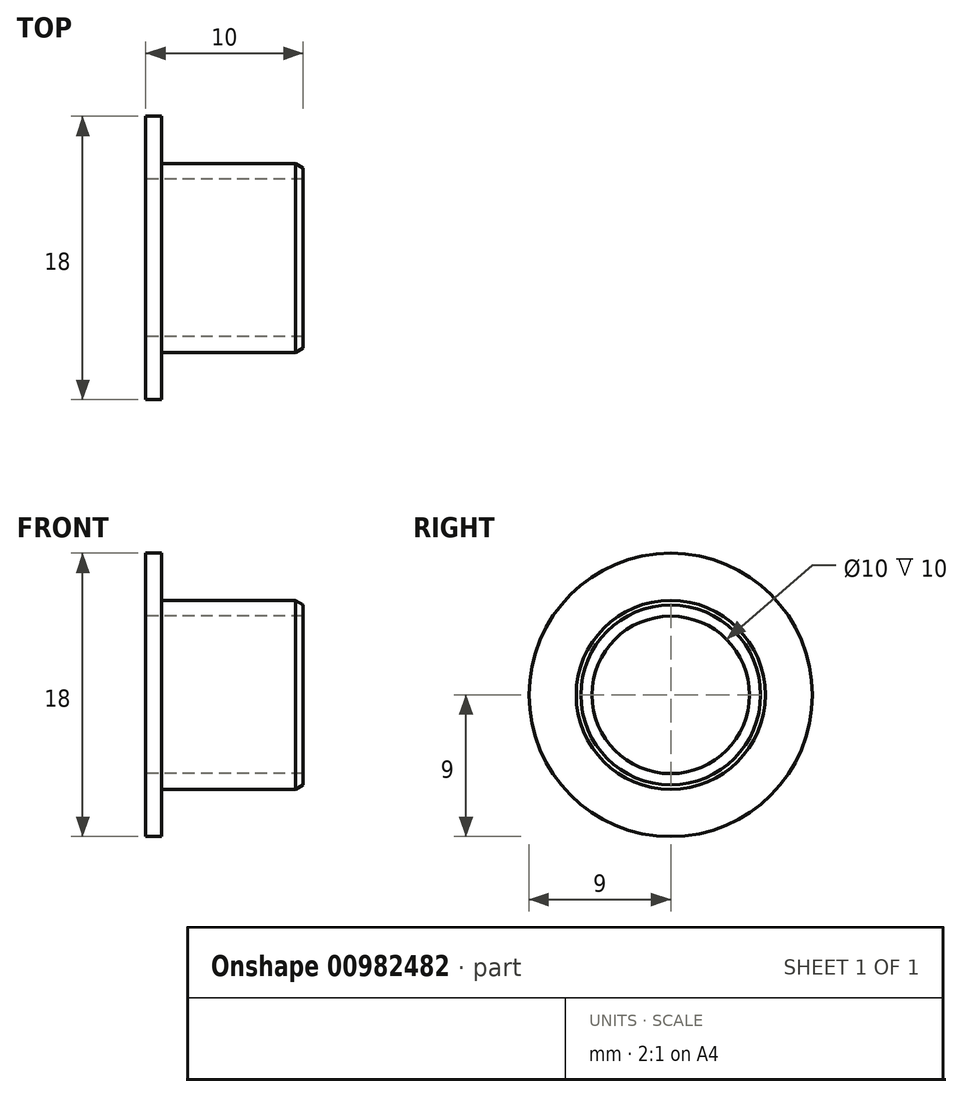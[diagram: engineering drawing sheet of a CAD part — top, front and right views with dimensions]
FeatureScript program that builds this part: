
annotation { "Feature Type Name" : "Feature", "Feature Type Description" : "" }
export const myFeature = defineFeature(function(context is Context, id is Id, definition is map)
    precondition{}
    {
        {
            var Q0;
            Q0=qCreatedBy(makeId("Front.planeOp"),FACE);
            var sketch = newSketch(context, id + "F0", { "sketchPlane" : qUnion([Q0])});
            skLineSegment(sketch, "E0", {"start": v(-14.71, 0) * mm, "end": v(17.2, 0) * mm, "construction": true});
            skLineSegment(sketch, "E1", {"start": v(-1, 9) * mm, "end": v(-1, 5) * mm});
            skLineSegment(sketch, "E2", {"start": v(-1, 5) * mm, "end": v(9, 5) * mm});
            skLineSegment(sketch, "E3", {"start": v(-1, 9) * mm, "end": v(0, 9) * mm});
            skLineSegment(sketch, "E4", {"start": v(0, 9) * mm, "end": v(0, 6) * mm});
            skLineSegment(sketch, "E5", {"start": v(0, 6) * mm, "end": v(8.5, 6) * mm});
            skLineSegment(sketch, "E6", {"start": v(8.5, 6) * mm, "end": v(9, 5.71) * mm});
            skLineSegment(sketch, "E7", {"start": v(9, 5.71) * mm, "end": v(9, 5) * mm});
            skSolve(sketch);
        }
        {
            var Q0;
            Q0=qSketchRegion(id+"F0",true);
            var Q1;
            Q1=sQuery(id+"F0.wireOp",EDGE,"E0");
            revolve(context, id + "F1", {"surfaceOperationType" : NewSurfaceOperationType.NEW, "entities" : qUnion([Q0]), "axis" : qUnion([Q1]), "revolveType" : RevolveType.FULL});
        }
    });
